# Revit family: Bommel Bowl Lamp - Birch
name_source: partatom
category: Lighting Fixtures
units: mm (PartAtom-declared; Revit-internal decimal feet)

## family parameters
Always vertical = Yes
Cut with Voids When Loaded = No
Host = Ceiling
Light Source = Yes
OmniClass Number = 23.80.70.11
OmniClass Title = Luminaries for Internal Lighting
Part Type = Normal
Room Calculation Point = No
Round Connector Dimension = Use Diameter
Shared = No

## types (1)
- Bommel Bowl Lamp - Birch
    Area = 0
    BarCode = <None>
    Color Filter = 16777215
    Default Elevation = 0' - 0"
    Dimming Lamp Color Temperature Shift = <None>
    Height = 0
    IsExtendedWarranty = 0
    Light Source Symbol Length = 10' - 0"
    NominalHeight = 0
    NominalLength = 0
    NominalWidth = 0
    ReplacementCost = 0
    Spot Beam Angle = 30.00°
    Spot Field Angle = 90.00°
    Tilt Angle = 90.00°
    WarrantyDurationLabor = 0
    WarrantyDurationParts = 0
    WarrantyPeriod = 0
    Width = 0

## geometry (parser evidence)
native form markers: Sweep x2
no freeform markers — native parametric forms only
